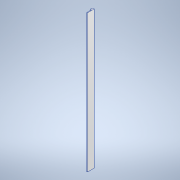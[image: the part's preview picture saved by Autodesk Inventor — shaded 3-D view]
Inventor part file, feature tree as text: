
AUTODESK INVENTOR PART (.ipt)
format: ipt  version: 2022 (Build 260153000, 153)  size: 100,864 bytes
history: native  units: mm
features: sketch x2, extrude x1
ambient origin geometry x8: Origin, YZ Plane, XZ Plane, XY Plane, X Axis, Y Axis, Z Axis, Center Point
bodies: Solid1 (feature_tree)
feature tree (3):
  sketch  "Sketch1"  dims[d0=44.0mm d1=6.0mm]
  extrude  "Extrusion1"  Depth=6.0mm
  sketch  "Sketch2"  dims[d2=10.0mm d3=65.0mm d4=1300.0mm d5=0.0mm]
